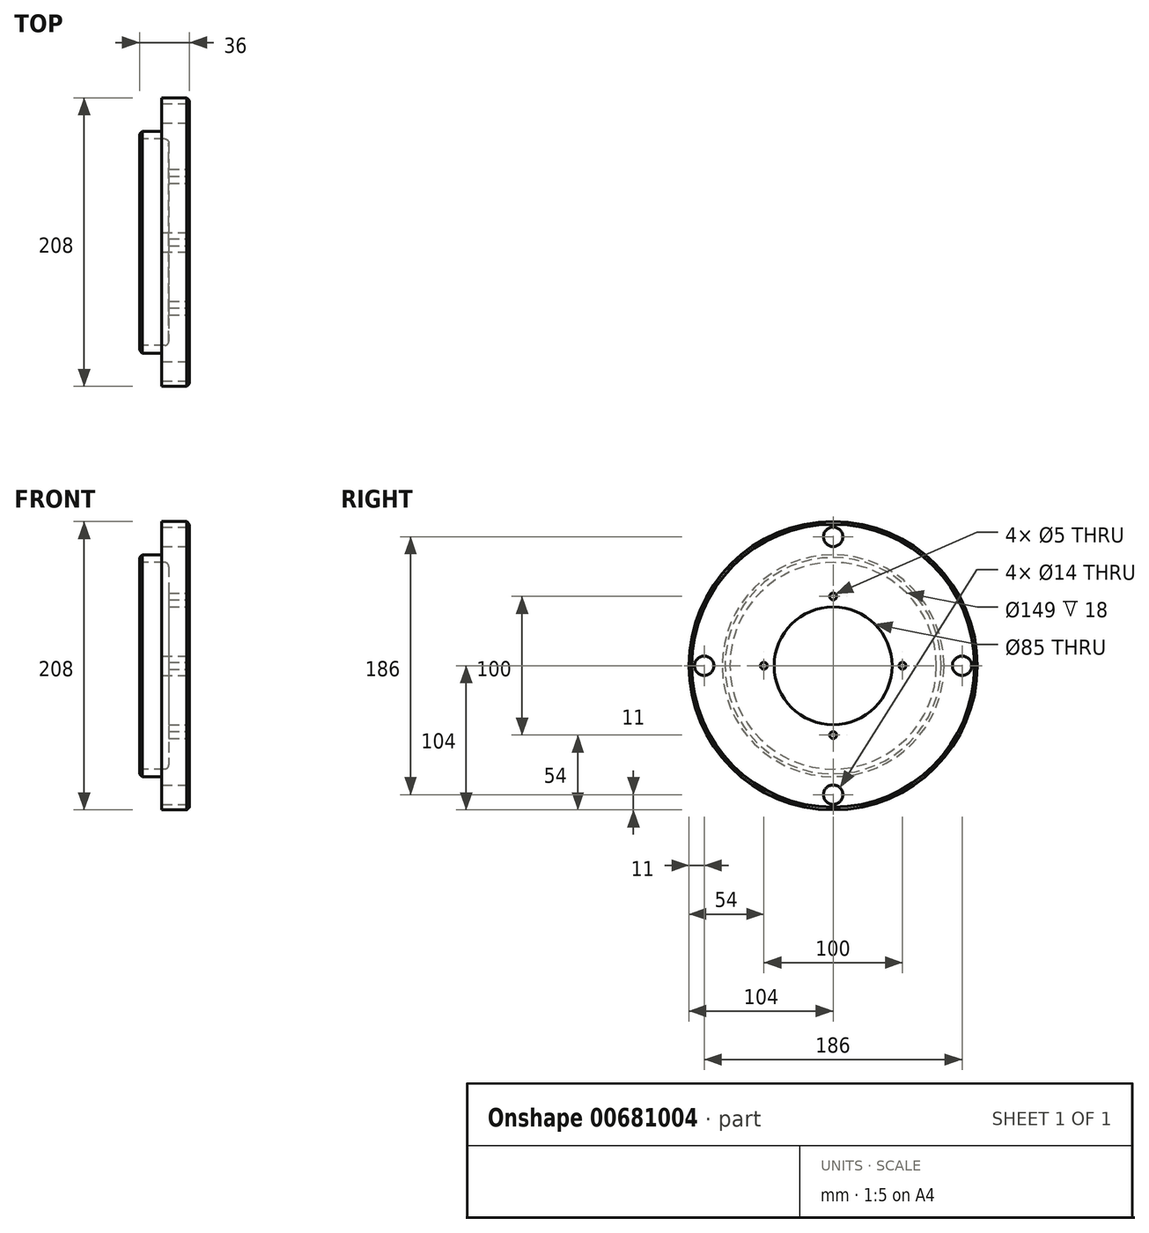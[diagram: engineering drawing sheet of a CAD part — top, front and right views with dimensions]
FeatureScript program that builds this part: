
annotation { "Feature Type Name" : "Feature", "Feature Type Description" : "" }
export const myFeature = defineFeature(function(context is Context, id is Id, definition is map)
    precondition{}
    {
        {
            var Q0;
            Q0=qCreatedBy(makeId("Right.planeOp"),FACE);
            var sketch = newSketch(context, id + "F0", { "sketchPlane" : qUnion([Q0])});
            skCircle(sketch, "E0", {"center": v(0, 0) * mm, "radius": 104 * mm});
            skSolve(sketch);
        }
        {
            var Q0;
            Q0=qSketchRegion(id+"F0",true);
            extrude(context, id + "F1", {"entities" : qUnion([Q0]), "depth" : 20 * mm, "offsetDistance" : 25 * mm});
        }
        {
            var Q0;
            Q0=makeQuery(id+"F1.opExtrude","CAP_FACE",FACE,{"disambiguationData":[OSD([sQuery(id+"F0.wireOp",EDGE,"E0")])],"isStart":true});
            var sketch = newSketch(context, id + "F2", { "sketchPlane" : qUnion([Q0])});
            skCircle(sketch, "E1", {"center": v(0, 0) * mm, "radius": 80 * mm});
            skSolve(sketch);
        }
        {
            var Q0;
            Q0=qSketchRegion(id+"F2",true);
            extrude(context, id + "F3", {"entities" : qUnion([Q0]), "operationType" : NewBodyOperationType.ADD, "depth" : 16 * mm, "offsetDistance" : 25 * mm});
        }
        {
            var Q0;
            Q0=makeQuery(id+"F3.opExtrude","CAP_EDGE",EDGE,{"disambiguationData":[OSD([sQuery(id+"F2.wireOp",EDGE,"E1")])],"isStart":false});
            var Q1;
            Q1=makeQuery(id+"F1.opExtrude","CAP_EDGE",EDGE,{"disambiguationData":[OSD([sQuery(id+"F0.wireOp",EDGE,"E0")])],"isStart":false});
            chamfer(context, id + "F4", {"entities" : qUnion([Q0, Q1]), "width" : 2 * mm, "tangentPropagation" : true});
        }
        {
            var Q0;
            Q0=makeQuery(id+"F3.opExtrude","CAP_FACE",FACE,{"disambiguationData":[OSD([sQuery(id+"F2.wireOp",EDGE,"E1")])],"isStart":false});
            var sketch = newSketch(context, id + "F5", { "sketchPlane" : qUnion([Q0])});
            skCircle(sketch, "E2", {"center": v(0, 0) * mm, "radius": 74.5 * mm});
            skSolve(sketch);
        }
        {
            var Q0;
            Q0=qSketchRegion(id+"F5",true);
            extrude(context, id + "F6", {"entities" : qUnion([Q0]), "operationType" : NewBodyOperationType.REMOVE, "oppositeDirection" : true, "depth" : 21 * mm, "offsetDistance" : 25 * mm});
        }
        {
            var Q0;
            Q0=makeQuery(id+"F6.boolean.opBoolean","COPY",EDGE,{"derivedFrom":makeQuery(id+"F6.opExtrude","CAP_EDGE",EDGE,{"disambiguationData":[OSD([sQuery(id+"F5.wireOp",EDGE,"E2")])],"isStart":false})});
            fillet(context, id + "F7", {"entities" : qUnion([Q0]), "radius" : 3 * mm, "tangentPropagation" : true, "allowEdgeOverflow" : false});
        }
        {
            var Q0;
            Q0=makeQuery(id+"F1.opExtrude","CAP_FACE",FACE,{"disambiguationData":[OSD([sQuery(id+"F0.wireOp",EDGE,"E0")])],"isStart":false});
            var sketch = newSketch(context, id + "F8", { "sketchPlane" : qUnion([Q0])});
            skPoint(sketch, "E3", {"position": v(0, 0) * mm});
            skSolve(sketch);
        }
        {
            var Q0;
            Q0=sQuery(id+"F8.wireOp",VERTEX,"E3");
            var Q1;
            Q1=makeQuery(id+"F1.opExtrude","SWEPT_BODY",BODY,{"disambiguationData":[OSD([sQuery(id+"F0.wireOp",EDGE,"E0")])]});
            hole(context, id + "F9", {"style" : HoleStyle.SIMPLE, "endStyle" : HoleEndStyle.THROUGH, "holeDiameter" : 85 * mm, "majorDiameter" : 5 * mm, "isTappedThrough" : true, "tappedDepth" : 24.75 * mm, "tapClearance" : 3, "locations" : qUnion([Q0]), "scope" : qUnion([Q1])});
        }
        {
            var Q0;
            Q0=makeQuery(id+"F1.opExtrude","CAP_FACE",FACE,{"disambiguationData":[OSD([sQuery(id+"F0.wireOp",EDGE,"E0")])],"isStart":false});
            var sketch = newSketch(context, id + "F10", { "sketchPlane" : qUnion([Q0])});
            skCircle(sketch, "E4", {"center": v(0, 0) * mm, "radius": 50 * mm, "construction": true});
            skLineSegment(sketch, "E5", {"start": v(0, 0) * mm, "end": v(0, 50) * mm, "construction": true});
            skPoint(sketch, "E6", {"position": v(0, 50) * mm});
            skPoint(sketch, "E7.1.0", {"position": v(-50, 0) * mm});
            skPoint(sketch, "E7.2.0", {"position": v(0, -50) * mm});
            skPoint(sketch, "E7.3.0", {"position": v(50, 0) * mm});
            skSolve(sketch);
        }
        {
            var Q0;
            Q0=sQuery(id+"F10.wireOp",VERTEX,"E6");
            var Q1;
            Q1=sQuery(id+"F10.wireOp",VERTEX,"E7.3.0");
            var Q2;
            Q2=sQuery(id+"F10.wireOp",VERTEX,"E7.2.0");
            var Q3;
            Q3=sQuery(id+"F10.wireOp",VERTEX,"E7.1.0");
            var Q4;
            Q4=makeQuery(id+"F1.opExtrude","SWEPT_BODY",BODY,{"disambiguationData":[OSD([sQuery(id+"F0.wireOp",EDGE,"E0")])]});
            hole(context, id + "F11", {"style" : HoleStyle.SIMPLE, "endStyle" : HoleEndStyle.THROUGH, "standardTappedOrClearance" : lookupTablePath({ "standard" : "ISO", "engagement" : "75%", "pitch" : "1 mm", "size" : "M6", "type" : "Tapped" }), "standardBlindInLast" : lookupTablePath({ "standard" : "ISO", "engagement" : "75%", "pitch" : "1 mm", "size" : "M6", "type" : "Tapped" }), "holeDiameter" : 5 * mm, "majorDiameter" : 6 * mm, "showTappedDepth" : true, "isTappedThrough" : true, "tappedDepth" : 24.75 * mm, "tapClearance" : 3, "locations" : qUnion([Q0, Q1, Q2, Q3]), "scope" : qUnion([Q4])});
        }
        {
            var Q0;
            Q0=makeQuery(id+"F1.opExtrude","CAP_FACE",FACE,{"disambiguationData":[OSD([sQuery(id+"F0.wireOp",EDGE,"E0")])],"isStart":false});
            var sketch = newSketch(context, id + "F12", { "sketchPlane" : qUnion([Q0])});
            skCircle(sketch, "E8", {"center": v(0, 0) * mm, "radius": 93 * mm, "construction": true});
            skLineSegment(sketch, "E9", {"start": v(0, 0) * mm, "end": v(0, 131.06) * mm, "construction": true});
            skPoint(sketch, "E10", {"position": v(0, 93) * mm});
            skPoint(sketch, "E11.1.0", {"position": v(-93, 0) * mm});
            skPoint(sketch, "E11.2.0", {"position": v(0, -93) * mm});
            skPoint(sketch, "E11.3.0", {"position": v(93, 0) * mm});
            skSolve(sketch);
        }
        {
            var Q0;
            Q0=sQuery(id+"F12.wireOp",VERTEX,"E10");
            var Q1;
            Q1=sQuery(id+"F12.wireOp",VERTEX,"E11.3.0");
            var Q2;
            Q2=sQuery(id+"F12.wireOp",VERTEX,"E11.2.0");
            var Q3;
            Q3=sQuery(id+"F12.wireOp",VERTEX,"E11.1.0");
            var Q4;
            Q4=makeQuery(id+"F1.opExtrude","SWEPT_BODY",BODY,{"disambiguationData":[OSD([sQuery(id+"F0.wireOp",EDGE,"E0")])]});
            hole(context, id + "F13", {"style" : HoleStyle.SIMPLE, "endStyle" : HoleEndStyle.THROUGH, "holeDiameter" : 14 * mm, "majorDiameter" : 6 * mm, "isTappedThrough" : true, "tappedDepth" : 24.75 * mm, "tapClearance" : 3, "locations" : qUnion([Q0, Q1, Q2, Q3]), "scope" : qUnion([Q4])});
        }
    });
